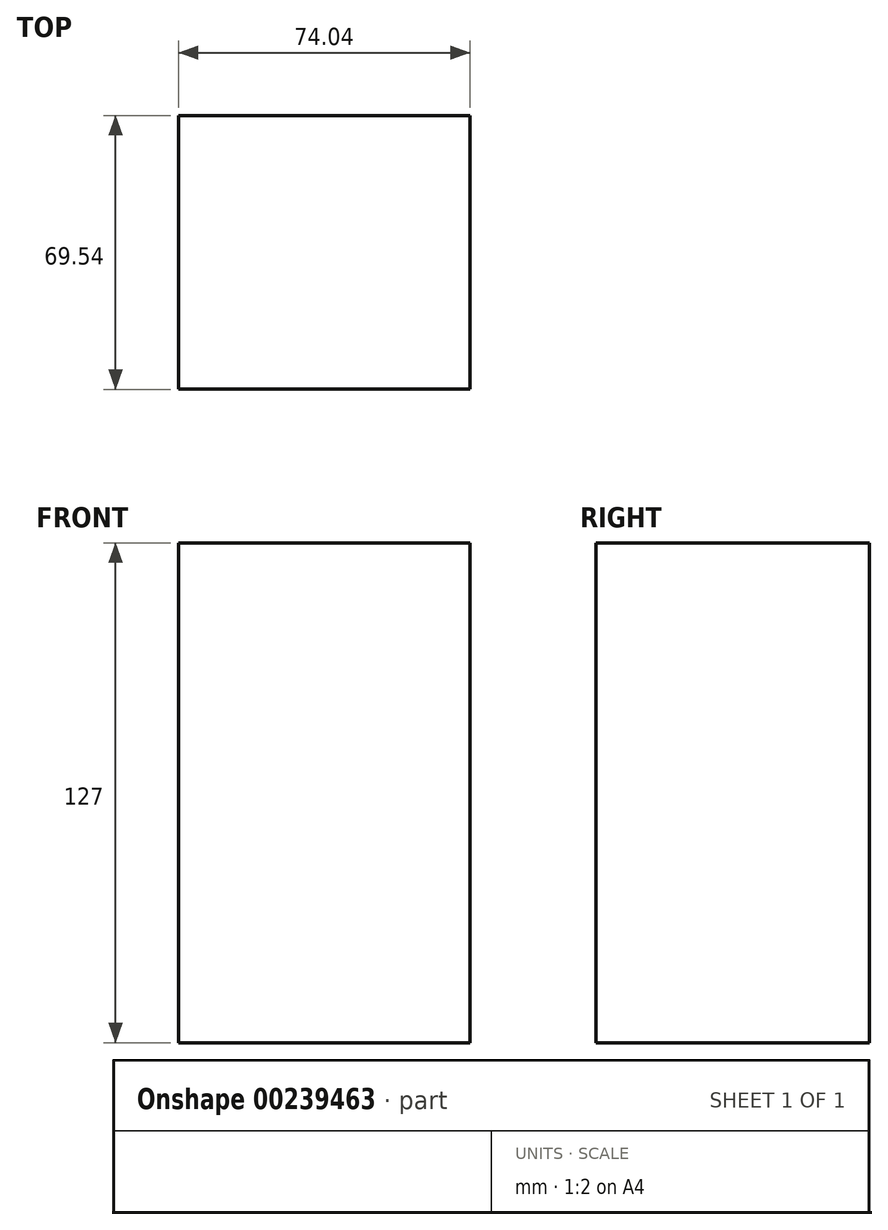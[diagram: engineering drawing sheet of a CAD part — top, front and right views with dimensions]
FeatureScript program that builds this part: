
annotation { "Feature Type Name" : "Feature", "Feature Type Description" : "" }
export const myFeature = defineFeature(function(context is Context, id is Id, definition is map)
    precondition{}
    {
        {
            var Q0;
            Q0=qCreatedBy(makeId("Top.planeOp"),FACE);
            var sketch = newSketch(context, id + "F0", { "sketchPlane" : qUnion([Q0])});
            skLineSegment(sketch, "E0.bottom", {"start": v(37.02, 34.77) * mm, "end": v(-37.02, 34.77) * mm});
            skLineSegment(sketch, "E0.top", {"start": v(37.02, -34.77) * mm, "end": v(-37.02, -34.77) * mm});
            skLineSegment(sketch, "E0.left", {"start": v(37.02, 34.77) * mm, "end": v(37.02, -34.77) * mm});
            skLineSegment(sketch, "E0.right", {"start": v(-37.02, 34.77) * mm, "end": v(-37.02, -34.77) * mm});
            skPoint(sketch, "E0.middle", {"position": v(0, 0) * mm});
            skSolve(sketch);
        }
        {
            var Q0;
            Q0 = qSketchRegion(id + "F0", true);
            extrude(context, id + "F1", {"entities" : qUnion([Q0]), "endBound" : BoundingType.SYMMETRIC, "depth" : 127 * mm});
        }
    });
